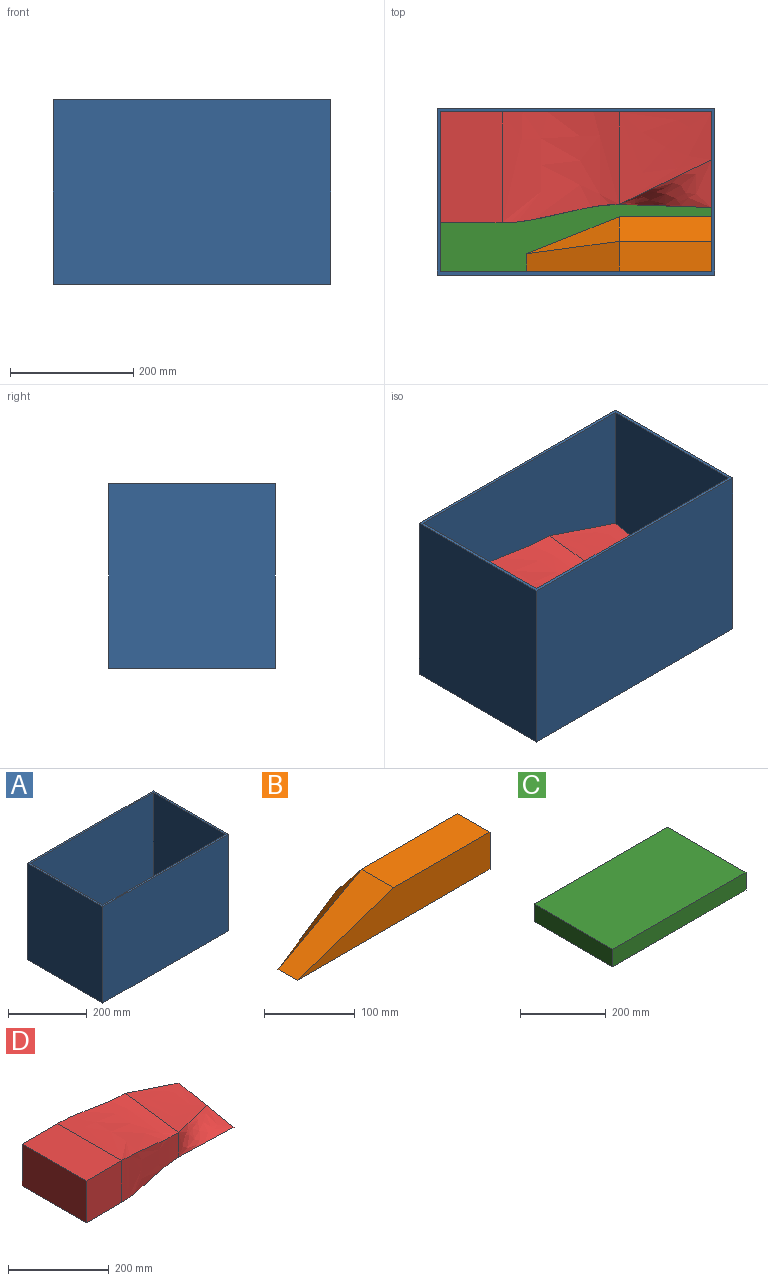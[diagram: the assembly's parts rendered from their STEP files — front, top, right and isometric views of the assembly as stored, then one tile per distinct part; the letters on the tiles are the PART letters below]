
ASSEMBLY  parts=4 mates=5
PART A: 11 faces, bbox 450x270x300 mm
  f0: plane 450x270mm, normal (0,0,1), area 7100mm2, adj f1,f2,f3,f4,f6,f7,f8,f9
  f1: plane 450x300mm, normal (0,-1,0), area 135000mm2, adj f0,f2,f4,f5
  f2: plane 300x270mm, normal (1,0,0), area 81000mm2, adj f0,f1,f3,f5
  f3: plane 450x300mm, normal (0,1,0), area 135000mm2, adj f0,f2,f4,f5
  f4: plane 300x270mm, normal (-1,0,0), area 81000mm2, adj f0,f1,f3,f5
  f5: plane 450x270mm, normal (0,0,-1), area 121500mm2, adj f1,f2,f3,f4
  f6: plane 440x295mm, normal (0,1,0), area 129800mm2, adj f0,f7,f9,f10
  f7: plane 295x260mm, normal (-1,0,0), area 76700mm2, adj f0,f6,f8,f10
  f8: plane 440x295mm, normal (0,-1,0), area 129800mm2, adj f0,f7,f9,f10
  f9: plane 295x260mm, normal (1,0,0), area 76700mm2, adj f0,f6,f8,f10
  f10: plane 440x260mm, normal (0,0,1), area 114400mm2, adj f6,f7,f8,f9
PART B: 7 faces, bbox 300x90x50 mm
  f0: plane 90x50mm, normal (1,0,0), area 3500mm2, adj f1,f2,f3,f4
  f1: plane 300x50mm, normal (0,-1,0), area 11250mm2, adj f0,f2,f3,f6
  f2: plane 150x50mm, normal (0,0,1), area 7500mm2, adj f0,f1,f4,f6
  f3: plane 300x90mm, normal (0,0,-1), area 22500mm2, adj f0,f1,f4,f5,f6
  f4: plane 150x50mm, normal (0,0.78,0.62), area 9604.7mm2, adj f0,f2,f3,f5
  f5: plane 150x60mm, normal (-0.3,0.75,0.6), area 5031.2mm2, adj f3,f4,f6
  f6: plane 150x50mm, normal (-0.32,0,0.95), area 6324.6mm2, adj f1,f2,f3,f5
PART C: 6 faces, bbox 440x260x50 mm
  f0: plane 440x50mm, normal (0,-1,0), area 22000mm2, adj f1,f3,f4,f5
  f1: plane 260x50mm, normal (1,0,0), area 13000mm2, adj f0,f2,f4,f5
  f2: plane 440x50mm, normal (0,1,0), area 22000mm2, adj f1,f3,f4,f5
  f3: plane 260x50mm, normal (-1,0,0), area 13000mm2, adj f0,f2,f4,f5
  f4: plane 440x260mm, normal (0,0,1), area 114400mm2, adj f0,f1,f2,f3
  f5: plane 440x260mm, normal (0,0,-1), area 114400mm2, adj f0,f1,f2,f3
PART D: 10 faces, bbox 440x180x101.6 mm
  f0: plane 101.6x100mm, normal (0,-1,0), area 10160mm2, adj f2,f3,f4,f5
  f1: plane 440x101.6mm, normal (0,1,0), area 35662mm2, adj f2,f3,f4,f6,f7,f8
  f2: plane 180x101.6mm, normal (-1,0,0), area 18288mm2, adj f0,f1,f3,f4
  f3: plane 180x100mm, normal (0,0,1), area 18000mm2, adj f0,f1,f2,f6
  f4: plane 440x180mm, normal (0,0,-1), area 72225mm2, adj f0,f1,f2,f5,f7,f9
  f5: bspline ~190x101.6mm, area 15579.4mm2, adj f0,f4,f6,f9
  f6: bspline ~190x180mm, area 32003.2mm2, adj f1,f3,f5,f8
  f7: plane 155x30mm, normal (1,0,0), area 2325mm2, adj f1,f4,f8,f9
  f8: bspline ~150x150mm, area 18291.7mm2, adj f1,f6,f7,f9
  f9: bspline ~150x77.5mm, area 9246.9mm2, adj f4,f5,f7,f8
PLACE A t=(4.52,-0.13,-4.09)mm fixed
PLACE B t=(4.52,-0.13,45.91)mm
PLACE C t=(4.52,-0.13,-4.09)mm
PLACE D t=(4.52,-0.13,45.91)mm
MATE planar D.f4 <-> C.f4  axis (0,0,-1) through (-215.48,129.87,45.91)mm
MATE planar D.f1 <-> A.f8  axis (0,1,0) through (-27.28,129.87,89.3)mm
MATE fastened B.f0 <-> C.f1  axis (-1,0,0) through (224.52,-130.13,45.91)mm
MATE fastened A.f5 <-> C.f5  axis (0,0,-1) through (4.52,-0.13,-4.09)mm
MATE planar D.f2 <-> A.f9  axis (-1,0,0) through (-215.48,39.87,96.71)mm
